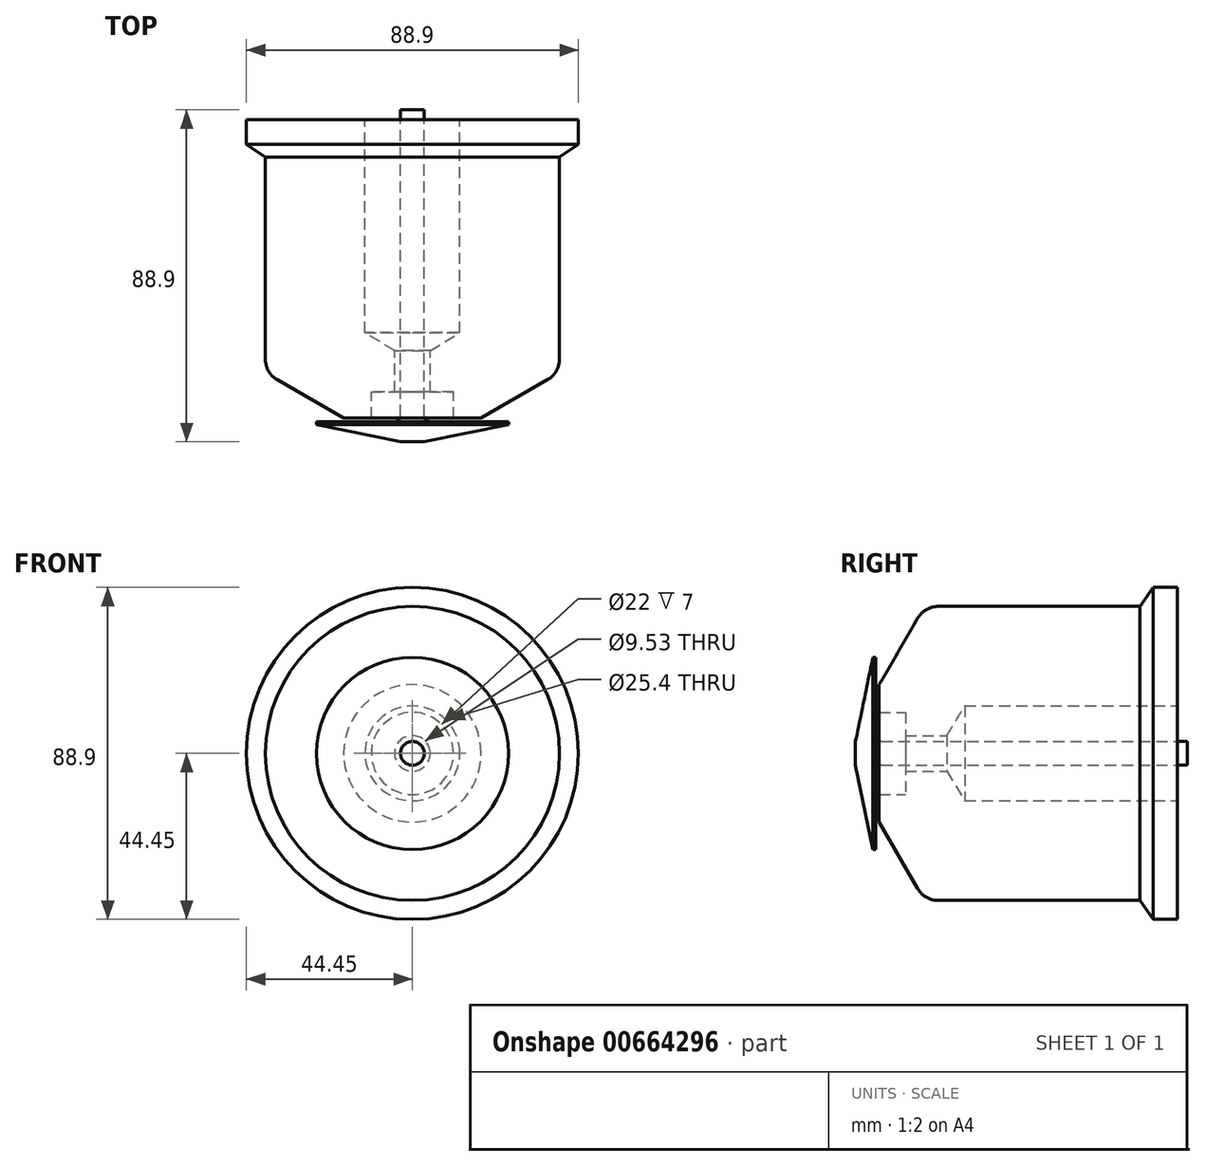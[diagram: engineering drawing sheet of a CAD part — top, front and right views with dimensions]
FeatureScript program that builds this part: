
annotation { "Feature Type Name" : "Feature", "Feature Type Description" : "" }
export const myFeature = defineFeature(function(context is Context, id is Id, definition is map)
    precondition{}
    {
        {
            var Q0;
            Q0=qCreatedBy(makeId("Right.planeOp"),FACE);
            var sketch = newSketch(context, id + "F0", { "sketchPlane" : qUnion([Q0])});
            skLineSegment(sketch, "E0", {"start": v(0, 39.37) * mm, "end": v(-54.08, 39.37) * mm});
            skLineSegment(sketch, "E1", {"start": v(-59.58, 36.2) * mm, "end": v(-69.85, 18.4) * mm});
            skLineSegment(sketch, "E2", {"start": v(-69.85, 18.4) * mm, "end": v(-69.85, 11) * mm});
            skLineSegment(sketch, "E3", {"start": v(-69.85, 11) * mm, "end": v(-62.85, 11) * mm});
            skLineSegment(sketch, "E4", {"start": v(-62.85, 11) * mm, "end": v(-62.85, 4.76) * mm});
            skLineSegment(sketch, "E5", {"start": v(-62.85, 4.76) * mm, "end": v(-51.75, 4.76) * mm});
            skLineSegment(sketch, "E6", {"start": v(-51.75, 4.76) * mm, "end": v(-46.98, 12.7) * mm});
            skLineSegment(sketch, "E7", {"start": v(-46.98, 12.7) * mm, "end": v(10.02, 12.7) * mm});
            skLineSegment(sketch, "E8", {"start": v(10.02, 12.7) * mm, "end": v(10.02, 44.45) * mm});
            skLineSegment(sketch, "E9", {"start": v(10.02, 44.45) * mm, "end": v(3.45, 44.45) * mm});
            skLineSegment(sketch, "E10", {"start": v(3.45, 44.45) * mm, "end": v(0, 39.37) * mm});
            skPoint(sketch, "E11.visualSharp", {"position": v(-57.74, 39.37) * mm});
            skArc(sketch, "E11.filletArc", {"start": v(-54.08, 39.37) * mm, "mid": v(-57.25, 38.52) * mm, "end": v(-59.58, 36.2) * mm});
            skLineSegment(sketch, "E12", {"start": v(0, 0) * mm, "end": v(-123.38, 0) * mm});
            skSolve(sketch);
        }
        {
            var Q0;
            Q0=makeQuery(id+"F0.imprint","IMPRINT",FACE,{"disambiguationData":[TD([[makeQuery(id+"F0.imprint","IMPRINT",EDGE,{"derivedFrom":sQuery(id+"F0.wireOp",EDGE,"E0")}),1.0]])]});
            var Q1;
            Q1=sQuery(id+"F0.wireOp",EDGE,"E12");
            revolve(context, id + "F1", {"entities" : qUnion([Q0]), "axis" : qUnion([Q1]), "revolveType" : RevolveType.FULL});
        }
        {
            var Q0;
            Q0=qCreatedBy(makeId("Right.planeOp"),FACE);
            var sketch = newSketch(context, id + "F2", { "sketchPlane" : qUnion([Q0])});
            skLineSegment(sketch, "E13", {"start": v(0, 0) * mm, "end": v(-76.2, 0) * mm});
            skLineSegment(sketch, "E14", {"start": v(-76.2, 3.18) * mm, "end": v(-71.56, 25.74) * mm});
            skLineSegment(sketch, "E15", {"start": v(-71.56, 25.74) * mm, "end": v(-70.8, 25.74) * mm});
            skLineSegment(sketch, "E16", {"start": v(-70.8, 25.74) * mm, "end": v(-70.8, 4.7) * mm});
            skLineSegment(sketch, "E17", {"start": v(-69.27, 3.17) * mm, "end": v(12.7, 3.18) * mm});
            skLineSegment(sketch, "E18", {"start": v(12.7, 3.18) * mm, "end": v(12.7, 0) * mm});
            skLineSegment(sketch, "E19", {"start": v(12.7, 0) * mm, "end": v(0, 0) * mm});
            skLineSegment(sketch, "E20", {"start": v(-76.2, 0) * mm, "end": v(-76.2, 3.18) * mm});
            skPoint(sketch, "E21.visualSharp", {"position": v(-70.8, 3.17) * mm});
            skArc(sketch, "E21.filletArc", {"start": v(-70.8, 4.7) * mm, "mid": v(-70.35, 3.62) * mm, "end": v(-69.27, 3.17) * mm});
            skSolve(sketch);
        }
        {
            var Q0;
            Q0=qCreatedBy(makeId("Right.planeOp"),FACE);
            var sketch = newSketch(context, id + "F3", { "sketchPlane" : qUnion([Q0])});
            skLineSegment(sketch, "E22", {"start": v(0, 0) * mm, "end": v(-162.15, 0) * mm});
            skSolve(sketch);
        }
        {
            var Q0;
            Q0 = qSketchRegion(id + "F2", true);
            var Q1;
            Q1=sQuery(id+"F3.wireOp",EDGE,"E22");
            revolve(context, id + "F4", {"entities" : qUnion([Q0]), "axis" : qUnion([Q1]), "revolveType" : RevolveType.FULL});
        }
    });
